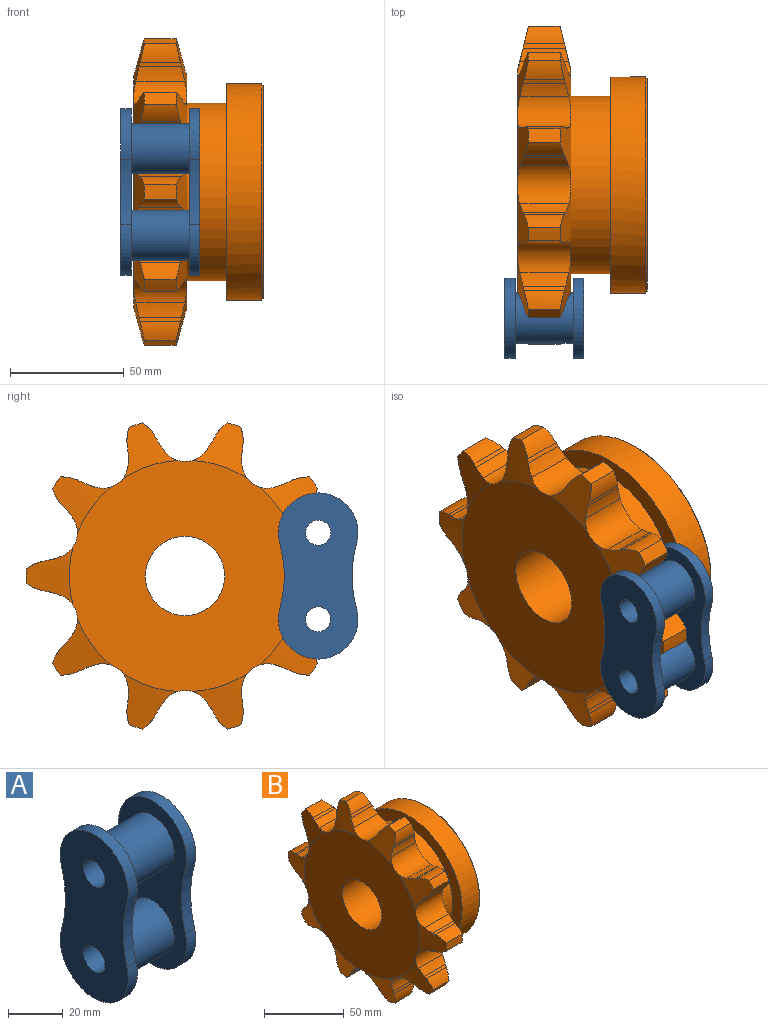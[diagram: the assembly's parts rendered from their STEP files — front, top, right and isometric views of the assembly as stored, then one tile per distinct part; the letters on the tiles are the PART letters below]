
ASSEMBLY  parts=2 mates=1
PART A: 16 faces, bbox 34.9x35.1x73.2 mm
  f0: plane 73.2x35.1mm, normal (1,0,0), area 1412mm2, adj f1,f2,f6,f7,f8,f9
  f1: cylinder r=17.55mm len=35.1mm, axis (-1,0,0), area 307.7mm2, adj f0,f2,f3,f6
  f2: cylinder r=52.69mm len=28.58mm, axis (-1,0,0), area 137.5mm2, adj f0,f1,f3,f7
  f3: plane 73.2x35.1mm, normal (-1,0,0), area 1994.4mm2, adj f1,f2,f4,f5,f6,f7
  f4: cylinder r=5.55mm len=34.9mm, axis (-1,0,0), area 1217mm2, adj f3,f15
  f5: cylinder r=5.55mm len=34.9mm, axis (-1,0,0), area 1217mm2, adj f3,f15
  f6: cylinder r=52.69mm len=28.58mm, axis (-1,0,0), area 137.5mm2, adj f0,f1,f3,f7
  f7: cylinder r=17.55mm len=35.1mm, axis (-1,0,0), area 307.7mm2, adj f0,f2,f3,f6
  f8: cylinder r=11.11mm len=25.4mm, axis (-1,0,0), area 1773.5mm2, adj f0,f10
  f9: cylinder r=11.11mm len=25.4mm, axis (-1,0,0), area 1773.5mm2, adj f0,f10
  f10: plane 73.2x35.1mm, normal (-1,0,0), area 1412mm2, adj f8,f9,f11,f12,f13,f14
  f11: cylinder r=52.69mm len=28.58mm, axis (1,0,0), area 137.5mm2, adj f10,f12,f14,f15
  f12: cylinder r=17.55mm len=35.1mm, axis (1,0,0), area 307.7mm2, adj f10,f11,f13,f15
  f13: cylinder r=52.69mm len=28.58mm, axis (1,0,0), area 137.5mm2, adj f10,f12,f14,f15
  f14: cylinder r=17.55mm len=35.1mm, axis (1,0,0), area 307.7mm2, adj f10,f11,f13,f15
  f15: plane 73.2x35.1mm, normal (1,0,0), area 1994.4mm2, adj f4,f5,f11,f12,f13,f14
PART B: 108 faces, bbox 57.2x140.1x139.9 mm
  f0: cone r=46.99mm half-angle=45deg, axis (-1,0,0), area 266.9mm2, adj f3,f10
  f1: cylinder r=39.2mm len=78.4mm, axis (-1,0,0), area 4335.3mm2, adj f11,f107
  f2: cylinder r=17.46mm len=57.15mm, axis (-1,0,0), area 6270.5mm2, adj f9,f10
  f3: cylinder r=47.62mm len=95.25mm, axis (-1,0,0), area 4621.2mm2, adj f0,f107
  f4: cylinder r=11.21mm len=23.47mm, axis (1,0,0), area 438mm2, adj f9,f11,f12,f13,f30,f31,f96,f97
  f5: cylinder r=11.21mm len=23.47mm, axis (1,0,0), area 437.4mm2, adj f9,f11,f13,f14,f31,f32,f90,f91
  f6: cylinder r=11.21mm len=23.47mm, axis (1,0,0), area 438mm2, adj f9,f11,f14,f15,f32,f33,f84,f85
  f7: cylinder r=18.96mm len=17.74mm, axis (1,0,0), area 137.4mm2, adj f17,f26,f35,f62
  f8: cylinder r=18.96mm len=17.74mm, axis (1,0,0), area 137.4mm2, adj f20,f29,f38,f54
  f9: plane 102.02x101.82mm, normal (-1,0,0), area 7192.1mm2, adj f2,f4,f5,f6,f30,f31,f32,f33
  f10: plane 93.98x93.98mm, normal (1,0,0), area 5978.8mm2, adj f0,f2
  f11: plane 102.02x101.82mm, normal (1,0,0), area 3322.8mm2, adj f1,f4,f5,f6,f12,f13,f14,f15
  f12: cone r=70.06mm half-angle=76deg, axis (-1,0,0), area 281.8mm2, adj f4,f11,f21,f94,f95,f96,f100,f101
  f13: cone r=70.06mm half-angle=76deg, axis (-1,0,0), area 283.5mm2, adj f4,f5,f11,f22,f88,f89,f90,f97
  f14: cone r=70.06mm half-angle=76deg, axis (-1,0,0), area 283.5mm2, adj f5,f6,f11,f23,f82,f83,f84,f91
  f15: cone r=70.06mm half-angle=76deg, axis (-1,0,0), area 281.8mm2, adj f6,f11,f24,f75,f76,f77,f78,f85
  f16: cone r=70.06mm half-angle=76deg, axis (-1,0,0), area 283.5mm2, adj f11,f25,f68,f69,f70,f71,f78,f79
  f17: cone r=70.06mm half-angle=76deg, axis (-1,0,0), area 281.2mm2, adj f7,f11,f26,f62,f63,f64,f71,f72
  f18: cone r=70.06mm half-angle=76deg, axis (-1,0,0), area 283.5mm2, adj f11,f27,f55,f56,f57,f58,f64,f65
  f19: cone r=70.06mm half-angle=76deg, axis (-1,0,0), area 283.5mm2, adj f11,f28,f49,f50,f51,f52,f58,f59
  f20: cone r=70.06mm half-angle=76deg, axis (-1,0,0), area 281.2mm2, adj f8,f11,f29,f45,f46,f47,f48,f52
  f21: cylinder r=70.06mm len=13.94mm, axis (-1,0,0), area 87mm2, adj f12,f30,f94,f100
  f22: cylinder r=70.06mm len=13.94mm, axis (-1,0,0), area 87mm2, adj f13,f31,f88,f99
  f23: cylinder r=70.06mm len=13.94mm, axis (-1,0,0), area 87mm2, adj f14,f32,f82,f93
  f24: cylinder r=70.06mm len=13.94mm, axis (-1,0,0), area 87mm2, adj f15,f33,f75,f87
  f25: cylinder r=70.06mm len=13.94mm, axis (-1,0,0), area 87mm2, adj f16,f34,f68,f81
  f26: cylinder r=70.06mm len=13.94mm, axis (-1,0,0), area 87mm2, adj f7,f17,f35,f74
  f27: cylinder r=70.06mm len=13.94mm, axis (-1,0,0), area 87mm2, adj f18,f36,f55,f67
  f28: cylinder r=70.06mm len=13.94mm, axis (-1,0,0), area 87mm2, adj f19,f37,f49,f61
  f29: cylinder r=70.06mm len=13.94mm, axis (-1,0,0), area 87mm2, adj f8,f20,f38,f48
  f30: cone r=51.01mm half-angle=76deg, axis (1,0,0), area 281.8mm2, adj f4,f9,f21,f94,f95,f96,f100,f101
  f31: cone r=51.01mm half-angle=76deg, axis (1,0,0), area 283.5mm2, adj f4,f5,f9,f22,f88,f89,f90,f97
  f32: cone r=51.01mm half-angle=76deg, axis (1,0,0), area 283.5mm2, adj f5,f6,f9,f23,f82,f83,f84,f91
  f33: cone r=51.01mm half-angle=76deg, axis (1,0,0), area 281.8mm2, adj f6,f9,f24,f75,f76,f77,f78,f85
  f34: cone r=51.01mm half-angle=76deg, axis (1,0,0), area 283.5mm2, adj f9,f25,f68,f69,f70,f71,f78,f79
  f35: cone r=51.01mm half-angle=76deg, axis (1,0,0), area 281.2mm2, adj f7,f9,f26,f62,f63,f64,f71,f72
  f36: cone r=51.01mm half-angle=76deg, axis (1,0,0), area 283.5mm2, adj f9,f27,f55,f56,f57,f58,f64,f65
  f37: cone r=51.01mm half-angle=76deg, axis (1,0,0), area 283.5mm2, adj f9,f28,f49,f50,f51,f52,f58,f59
  f38: cone r=51.01mm half-angle=76deg, axis (1,0,0), area 281.2mm2, adj f8,f9,f29,f45,f46,f47,f48,f52
  f39: cone r=70.06mm half-angle=76deg, axis (-1,0,0), area 283.5mm2, adj f11,f40,f42,f43,f44,f45,f103,f104
  f40: cylinder r=70.06mm len=13.94mm, axis (-1,0,0), area 87mm2, adj f39,f41,f42,f106
  f41: cone r=51.01mm half-angle=76deg, axis (1,0,0), area 283.5mm2, adj f9,f40,f42,f43,f44,f45,f103,f104
  f42: cylinder r=18.96mm len=17.74mm, axis (1,0,0), area 137.4mm2, adj f39,f40,f41,f43
  f43: plane 18.66x1.88mm, normal (0,-0.18,-0.98), area 34.7mm2, adj f39,f41,f42,f44
  f44: cylinder r=28.99mm len=21.5mm, axis (1,0,0), area 125.9mm2, adj f39,f41,f43,f45
  f45: cylinder r=11.21mm len=23.47mm, axis (1,0,0), area 437.4mm2, adj f9,f11,f20,f38,f39,f41,f44,f46
  f46: cylinder r=28.99mm len=21.5mm, axis (1,0,0), area 125.9mm2, adj f20,f38,f45,f47
  f47: plane 18.66x1.39mm, normal (0,-0.73,0.69), area 34.7mm2, adj f20,f38,f46,f48
  f48: cylinder r=18.96mm len=17.74mm, axis (1,0,0), area 137.4mm2, adj f20,f29,f38,f47
  f49: cylinder r=18.96mm len=17.74mm, axis (1,0,0), area 137.4mm2, adj f19,f28,f37,f50
  f50: plane 18.66x1.9mm, normal (0,-0.99,0.13), area 34.7mm2, adj f19,f37,f49,f51
  f51: cylinder r=28.99mm len=21.5mm, axis (1,0,0), area 125.9mm2, adj f19,f37,f50,f52
  f52: cylinder r=11.21mm len=23.47mm, axis (1,0,0), area 437.4mm2, adj f9,f11,f19,f20,f37,f38,f51,f53
  f53: cylinder r=28.99mm len=21.5mm, axis (1,0,0), area 125.9mm2, adj f20,f38,f52,f54
  f54: plane 18.66x1.73mm, normal (0,0.43,-0.9), area 34.7mm2, adj f8,f20,f38,f53
  f55: cylinder r=18.96mm len=17.74mm, axis (1,0,0), area 137.4mm2, adj f18,f27,f36,f56
  f56: plane 18.66x1.68mm, normal (0,-0.88,-0.48), area 34.7mm2, adj f18,f36,f55,f57
  f57: cylinder r=28.99mm len=21.5mm, axis (1,0,0), area 125.9mm2, adj f18,f36,f56,f58
  f58: cylinder r=11.21mm len=23.47mm, axis (1,0,0), area 437.4mm2, adj f9,f11,f18,f19,f36,f37,f57,f59
  f59: cylinder r=28.99mm len=21.5mm, axis (1,0,0), area 125.9mm2, adj f19,f37,f58,f60
  f60: plane 18.66x1.68mm, normal (0,0.88,-0.48), area 34.7mm2, adj f19,f37,f59,f61
  f61: cylinder r=18.96mm len=17.74mm, axis (1,0,0), area 137.4mm2, adj f19,f28,f37,f60
  f62: plane 18.66x1.73mm, normal (0,-0.43,-0.9), area 34.7mm2, adj f7,f17,f35,f63
  f63: cylinder r=28.99mm len=21.5mm, axis (1,0,0), area 125.9mm2, adj f17,f35,f62,f64
  f64: cylinder r=11.21mm len=23.47mm, axis (1,0,0), area 437.4mm2, adj f9,f11,f17,f18,f35,f36,f63,f65
  f65: cylinder r=28.99mm len=21.5mm, axis (1,0,0), area 125.9mm2, adj f18,f36,f64,f66
  f66: plane 18.66x1.9mm, normal (0,0.99,0.13), area 34.7mm2, adj f18,f36,f65,f67
  f67: cylinder r=18.96mm len=17.74mm, axis (1,0,0), area 137.4mm2, adj f18,f27,f36,f66
  f68: cylinder r=18.96mm len=17.74mm, axis (1,0,0), area 137.4mm2, adj f16,f25,f34,f69
  f69: plane 18.66x1.88mm, normal (0,0.18,-0.98), area 34.7mm2, adj f16,f34,f68,f70
  f70: cylinder r=28.99mm len=21.5mm, axis (1,0,0), area 125.9mm2, adj f16,f34,f69,f71
  f71: cylinder r=11.21mm len=23.47mm, axis (1,0,0), area 437.4mm2, adj f9,f11,f16,f17,f34,f35,f70,f72
  f72: cylinder r=28.99mm len=21.5mm, axis (1,0,0), area 125.9mm2, adj f17,f35,f71,f73
  f73: plane 18.66x1.39mm, normal (0,0.73,0.69), area 34.7mm2, adj f17,f35,f72,f74
  f74: cylinder r=18.96mm len=17.74mm, axis (1,0,0), area 137.4mm2, adj f17,f26,f35,f73
  f75: cylinder r=18.96mm len=17.74mm, axis (1,0,0), area 137.4mm2, adj f15,f24,f33,f76
  f76: plane 18.66x1.39mm, normal (0,0.73,-0.69), area 34.7mm2, adj f15,f33,f75,f77
  f77: cylinder r=28.99mm len=21.5mm, axis (1,0,0), area 125.9mm2, adj f15,f33,f76,f78
  f78: cylinder r=11.21mm len=23.47mm, axis (1,0,0), area 437.4mm2, adj f9,f11,f15,f16,f33,f34,f77,f79
  f79: cylinder r=28.99mm len=21.5mm, axis (1,0,0), area 125.9mm2, adj f16,f34,f78,f80
  f80: plane 18.66x1.88mm, normal (0,0.18,0.98), area 34.7mm2, adj f16,f34,f79,f81
  f81: cylinder r=18.96mm len=17.74mm, axis (1,0,0), area 137.4mm2, adj f16,f25,f34,f80
  f82: cylinder r=18.96mm len=17.74mm, axis (1,0,0), area 137.4mm2, adj f14,f23,f32,f83
  f83: plane 18.66x1.9mm, normal (0,0.99,-0.13), area 34.7mm2, adj f14,f32,f82,f84
  f84: cylinder r=28.99mm len=21.5mm, axis (1,0,0), area 125.9mm2, adj f6,f14,f32,f83
  f85: cylinder r=28.99mm len=21.5mm, axis (1,0,0), area 125.9mm2, adj f6,f15,f33,f86
  f86: plane 18.66x1.73mm, normal (0,-0.43,0.9), area 34.7mm2, adj f15,f33,f85,f87
  f87: cylinder r=18.96mm len=17.74mm, axis (1,0,0), area 137.4mm2, adj f15,f24,f33,f86
  f88: cylinder r=18.96mm len=17.74mm, axis (1,0,0), area 137.4mm2, adj f13,f22,f31,f89
  f89: plane 18.66x1.68mm, normal (0,0.88,0.48), area 34.7mm2, adj f13,f31,f88,f90
  f90: cylinder r=28.99mm len=21.5mm, axis (1,0,0), area 125.9mm2, adj f5,f13,f31,f89
  f91: cylinder r=28.99mm len=21.5mm, axis (1,0,0), area 125.9mm2, adj f5,f14,f32,f92
  f92: plane 18.66x1.68mm, normal (0,-0.88,0.48), area 34.7mm2, adj f14,f32,f91,f93
  f93: cylinder r=18.96mm len=17.74mm, axis (1,0,0), area 137.4mm2, adj f14,f23,f32,f92
  f94: cylinder r=18.96mm len=17.74mm, axis (1,0,0), area 137.4mm2, adj f12,f21,f30,f95
  f95: plane 18.66x1.73mm, normal (0,0.43,0.9), area 34.7mm2, adj f12,f30,f94,f96
  f96: cylinder r=28.99mm len=21.5mm, axis (1,0,0), area 125.9mm2, adj f4,f12,f30,f95
  f97: cylinder r=28.99mm len=21.5mm, axis (1,0,0), area 125.9mm2, adj f4,f13,f31,f98
  f98: plane 18.66x1.9mm, normal (0,-0.99,-0.13), area 34.7mm2, adj f13,f31,f97,f99
  f99: cylinder r=18.96mm len=17.74mm, axis (1,0,0), area 137.4mm2, adj f13,f22,f31,f98
  f100: cylinder r=18.96mm len=17.74mm, axis (1,0,0), area 137.4mm2, adj f12,f21,f30,f101
  f101: plane 18.66x1.39mm, normal (0,-0.73,-0.69), area 34.7mm2, adj f12,f30,f100,f102
  f102: cylinder r=28.99mm len=21.5mm, axis (1,0,0), area 125.9mm2, adj f12,f30,f101,f103
  f103: cylinder r=11.21mm len=23.47mm, axis (1,0,0), area 437.4mm2, adj f9,f11,f12,f30,f39,f41,f102,f104
  f104: cylinder r=28.99mm len=21.5mm, axis (1,0,0), area 125.9mm2, adj f39,f41,f103,f105
  f105: plane 18.66x1.88mm, normal (0,-0.18,0.98), area 34.7mm2, adj f39,f41,f104,f106
  f106: cylinder r=18.96mm len=17.74mm, axis (1,0,0), area 137.4mm2, adj f39,f40,f41,f105
  f107: plane 95.25x95.25mm, normal (-1,0,0), area 2298.4mm2, adj f1,f3
PLACE A t=(0,-58.63,0)mm
PLACE B at identity fixed
MATE revolute A.f9 <-> B.f103  axis (-1,0,0) through (0,-58.63,19.05)mm
